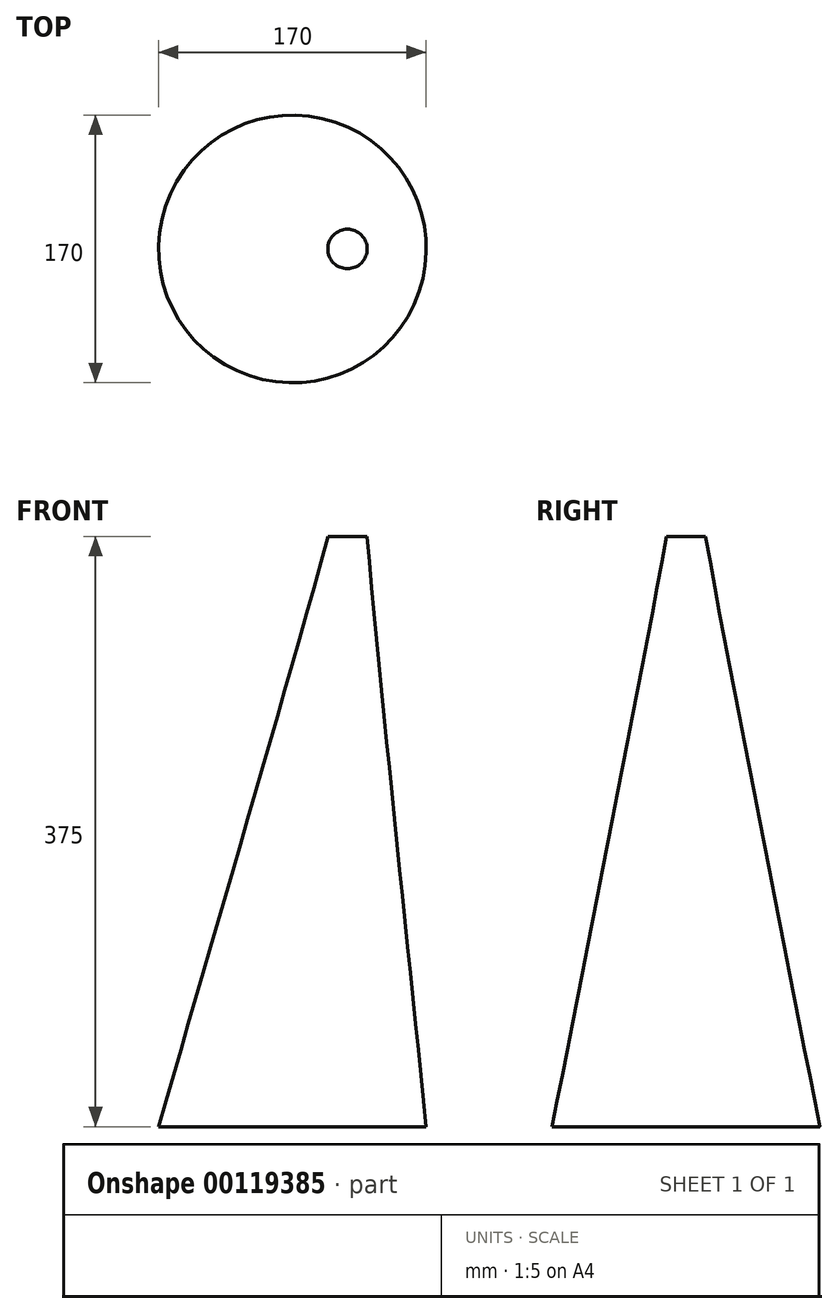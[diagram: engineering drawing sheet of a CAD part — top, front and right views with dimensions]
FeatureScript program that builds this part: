
annotation { "Feature Type Name" : "Feature", "Feature Type Description" : "" }
export const myFeature = defineFeature(function(context is Context, id is Id, definition is map)
    precondition{}
    {
        {
            var Q0;
            Q0=qCreatedBy(makeId("Top.planeOp"),FACE);
            var sketch = newSketch(context, id + "F0", { "sketchPlane" : qUnion([Q0])});
            skPoint(sketch, "E0.middle", {"position": v(0, 0) * mm});
            skCircle(sketch, "E1", {"center": v(0, 0) * mm, "radius": 85 * mm});
            skSolve(sketch);
        }
        {
            var Q0;
            Q0=qCreatedBy(makeId("Top.planeOp"),FACE);
            cPlane(context, id + "F1", {"entities" : qUnion([Q0]), "cplaneType" : CPlaneType.OFFSET, "offset" : 375 * mm, "width" : 150 * mm, "height" : 150 * mm});
        }
        {
            var Q0;
            Q0=qCreatedBy(id+"F1.planeOp",FACE);
            var sketch = newSketch(context, id + "F2", { "sketchPlane" : qUnion([Q0])});
            skPoint(sketch, "E2.middle", {"position": v(35, 0) * mm});
            skLineSegment(sketch, "E3", {"start": v(35, 0) * mm, "end": v(26.16, -8.84) * mm, "construction": true});
            skLineSegment(sketch, "E4", {"start": v(35, 0) * mm, "end": v(26.16, 8.84) * mm, "construction": true});
            skLineSegment(sketch, "E5", {"start": v(35, 0) * mm, "end": v(43.84, 8.84) * mm, "construction": true});
            skLineSegment(sketch, "E6", {"start": v(35, 0) * mm, "end": v(43.84, -8.84) * mm, "construction": true});
            skArc(sketch, "E7", {"start": v(26.16, -8.84) * mm, "mid": v(35, -12.5) * mm, "end": v(43.84, -8.84) * mm});
            skArc(sketch, "E8", {"start": v(43.84, -8.84) * mm, "mid": v(47.5, 0) * mm, "end": v(43.84, 8.84) * mm});
            skLineSegment(sketch, "E9", {"start": v(43.84, 8.84) * mm, "end": v(43.84, 8.84) * mm});
            skArc(sketch, "E10", {"start": v(26.16, 8.84) * mm, "mid": v(22.5, 0) * mm, "end": v(26.16, -8.84) * mm});
            skArc(sketch, "E11", {"start": v(43.84, 8.84) * mm, "mid": v(35, 12.5) * mm, "end": v(26.16, 8.84) * mm});
            skSolve(sketch);
        }
        {
            var Q0;
            Q0=makeQuery(id+"F0.imprint","IMPRINT",FACE,{"disambiguationData":[TD([[makeQuery(id+"F0.imprint","IMPRINT",EDGE,{"derivedFrom":sQuery(id+"F0.wireOp",EDGE,"E1")}),1.0]])]});
            var Q1;
            Q1 = qSketchRegion(id + "F2", true);
            loft(context, id + "F3", {"sheetProfilesArray" : [{ "sheetProfileEntities" : qUnion([Q0]) }, { "sheetProfileEntities" : qUnion([Q1]) }]});
        }
    });
